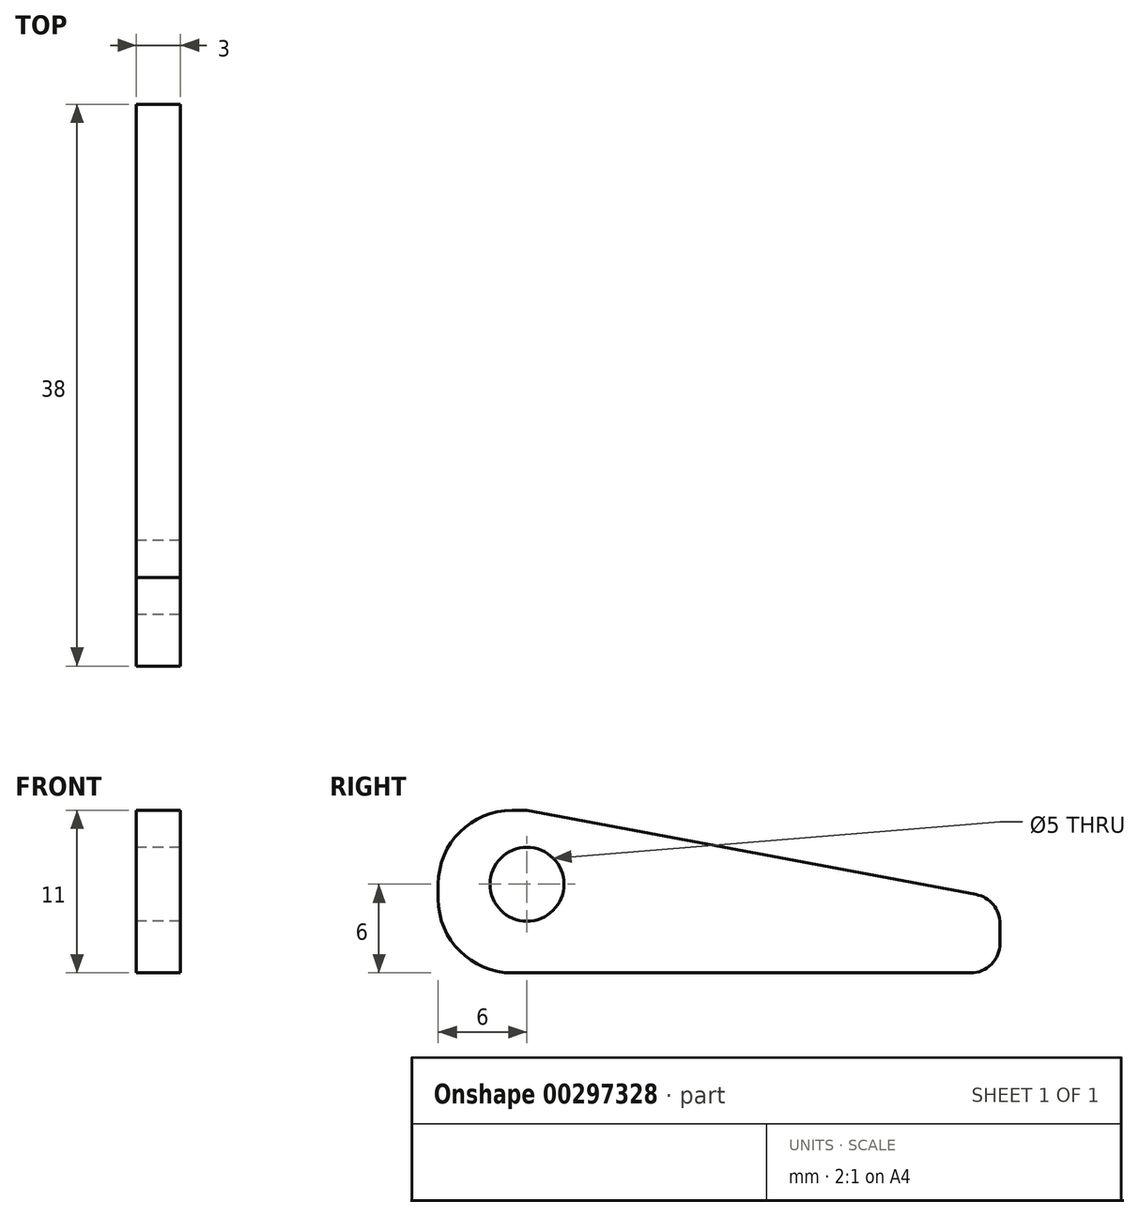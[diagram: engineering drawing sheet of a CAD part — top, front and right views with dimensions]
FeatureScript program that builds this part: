
annotation { "Feature Type Name" : "Feature", "Feature Type Description" : "" }
export const myFeature = defineFeature(function(context is Context, id is Id, definition is map)
    precondition{}
    {
        {
            var Q0;
            Q0=qCreatedBy(makeId("Right.planeOp"),FACE);
            var sketch = newSketch(context, id + "F0", { "sketchPlane" : qUnion([Q0])});
            skLineSegment(sketch, "E0", {"start": v(-19, 0) * mm, "end": v(19, 0) * mm});
            skLineSegment(sketch, "E1", {"start": v(19, 0) * mm, "end": v(19, 5) * mm});
            skLineSegment(sketch, "E2", {"start": v(19, 5) * mm, "end": v(-13, 11) * mm});
            skLineSegment(sketch, "E3", {"start": v(-19, 11) * mm, "end": v(-19, 0) * mm});
            skCircle(sketch, "E4", {"center": v(-13, 6) * mm, "radius": 2.5 * mm});
            skPoint(sketch, "E4.centerSnap0", {"position": v(-18.5, 6) * mm});
            skLineSegment(sketch, "E5", {"start": v(-19, 11) * mm, "end": v(-13, 11) * mm});
            skSolve(sketch);
        }
        {
            var Q0;
            Q0 = qSketchRegion(id + "F0", true);
            extrude(context, id + "F1", {"entities" : qUnion([Q0]), "depth" : 3 * mm});
        }
        {
            var Q0;
            Q0=makeQuery(id+"F1.opExtrude","SWEPT_EDGE",EDGE,{"disambiguationData":[OSD([sQuery(id+"F0.wireOp",EDGE,"E0"),sQuery(id+"F0.wireOp",EDGE,"E1")])]});
            fillet(context, id + "F2", {"entities" : qUnion([Q0]), "radius" : 2 * mm, "tangentPropagation" : true, "allowEdgeOverflow" : false});
        }
        {
            var Q0;
            Q0=makeQuery(id+"F1.opExtrude","SWEPT_EDGE",EDGE,{"disambiguationData":[OSD([sQuery(id+"F0.wireOp",EDGE,"E3"),sQuery(id+"F0.wireOp",EDGE,"E5")])]});
            var Q1;
            Q1=makeQuery(id+"F1.opExtrude","SWEPT_EDGE",EDGE,{"disambiguationData":[OSD([sQuery(id+"F0.wireOp",EDGE,"E0"),sQuery(id+"F0.wireOp",EDGE,"E3")])]});
            fillet(context, id + "F3", {"entities" : qUnion([Q0, Q1]), "radius" : 5 * mm, "tangentPropagation" : true, "allowEdgeOverflow" : false});
        }
        {
            var Q0;
            Q0=makeQuery(id+"F1.opExtrude","SWEPT_EDGE",EDGE,{"disambiguationData":[OSD([sQuery(id+"F0.wireOp",EDGE,"E1"),sQuery(id+"F0.wireOp",EDGE,"E2")])]});
            fillet(context, id + "F4", {"entities" : qUnion([Q0]), "radius" : 2 * mm, "tangentPropagation" : true, "allowEdgeOverflow" : false});
        }
    });
